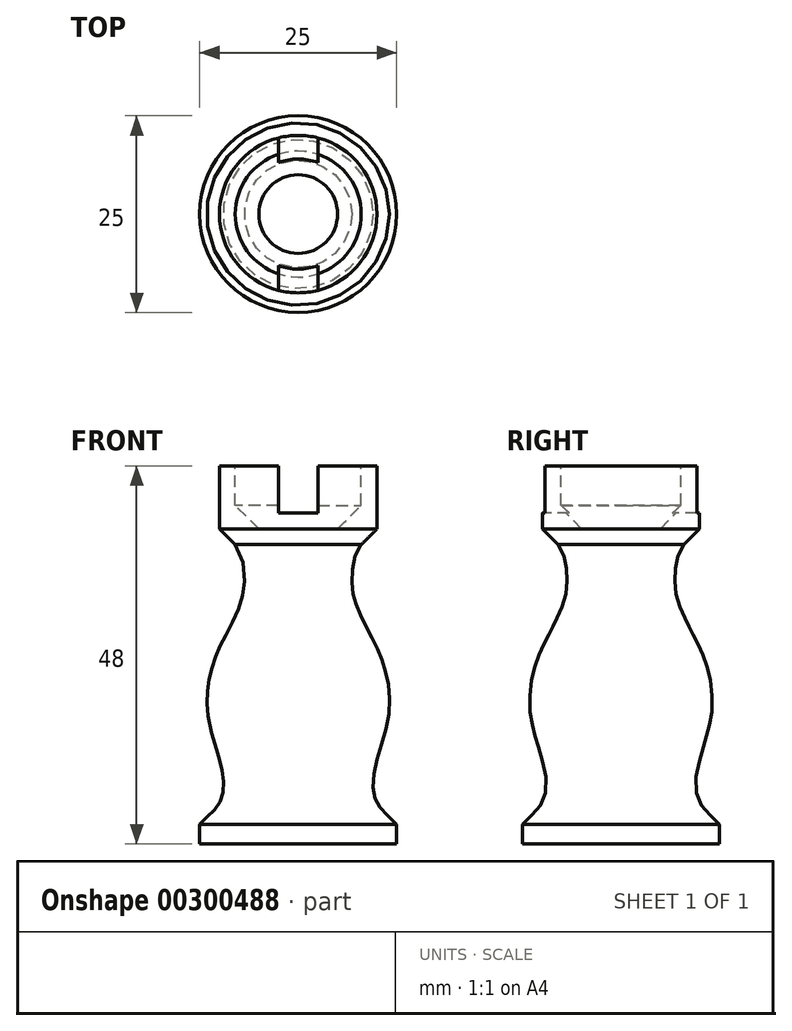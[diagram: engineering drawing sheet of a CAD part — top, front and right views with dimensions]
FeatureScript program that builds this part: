
annotation { "Feature Type Name" : "Feature", "Feature Type Description" : "" }
export const myFeature = defineFeature(function(context is Context, id is Id, definition is map)
    precondition{}
    {
        {
            var Q0;
            Q0=qCreatedBy(makeId("Front.planeOp"),FACE);
            var sketch = newSketch(context, id + "F0", { "sketchPlane" : qUnion([Q0])});
            skLineSegment(sketch, "E0.bottom", {"start": v(0, 0) * mm, "end": v(12.5, 0) * mm});
            skLineSegment(sketch, "E0.top", {"start": v(0, 48) * mm, "end": v(12.5, 48) * mm});
            skLineSegment(sketch, "E0.left", {"start": v(0, 0) * mm, "end": v(0, 48) * mm});
            skLineSegment(sketch, "E0.right", {"start": v(12.5, 0) * mm, "end": v(12.5, 48) * mm});
            skLineSegment(sketch, "E1.bottom", {"start": v(0, 48) * mm, "end": v(8, 48) * mm});
            skLineSegment(sketch, "E1.top", {"start": v(0, 40) * mm, "end": v(8, 40) * mm});
            skLineSegment(sketch, "E1.left", {"start": v(0, 48) * mm, "end": v(0, 40) * mm});
            skLineSegment(sketch, "E1.right", {"start": v(8, 48) * mm, "end": v(8, 40) * mm});
            skLineSegment(sketch, "E2", {"start": v(10, 48) * mm, "end": v(10, 38) * mm});
            skLineSegment(sketch, "E3", {"start": v(10, 38) * mm, "end": v(0, 38) * mm});
            skLineSegment(sketch, "E4", {"start": v(10, 40) * mm, "end": v(8, 38) * mm});
            skLineSegment(sketch, "E5", {"start": v(0, 2.5) * mm, "end": v(12.5, 2.5) * mm});
            skFitSpline(sketch, "E6", {"points": [v(8, 38) * mm, v(6.84, 33.3) * mm, v(7.56, 29.92) * mm, v(9.58, 25.78) * mm, v(11.1, 21.87) * mm, v(11.46, 16.18) * mm, v(9.68, 9.37) * mm, v(10, 5.2) * mm, v(12.5, 2.5) * mm], "startDerivative": vector(-23.17, -26.5) * mm, "endDerivative": vector(26.84, -29.85) * mm});
            skSolve(sketch);
        }
        {
            var Q0;
            {var subQ0=sQuery(id+"F0.wireOp",EDGE,"E1.top");Q0=makeQuery(id+"F0.imprint","IMPRINT",FACE,{"disambiguationData":[TD([[makeQuery(id+"F0.imprint","IMPRINT",EDGE,{"derivedFrom":subQ0}),-1.0]])]});}
            var Q1;
            {var subQ3=sQuery(id+"F0.wireOp",EDGE,"E5");Q1=makeQuery(id+"F0.imprint","IMPRINT",FACE,{"disambiguationData":[TD([[makeQuery(id+"F0.imprint","IMPRINT",EDGE,{"derivedFrom":subQ3}),1.0]])]});}
            var Q2;
            {var subQ0=sQuery(id+"F0.wireOp",EDGE,"E0.bottom");Q2=makeQuery(id+"F0.imprint","IMPRINT",FACE,{"disambiguationData":[TD([[makeQuery(id+"F0.imprint","IMPRINT",EDGE,{"derivedFrom":subQ0}),1.0]])]});}
            var Q3;
            Q3=sQuery(id+"F0.wireOp",EDGE,"E1.left");
            revolve(context, id + "F1", {"entities" : qUnion([Q0, Q1, Q2]), "axis" : qUnion([Q3]), "revolveType" : RevolveType.FULL});
        }
        {
            var Q0;
            Q0=makeQuery(id+"F1.opRevolve","SWEPT_FACE",FACE,{"disambiguationData":[OSD([sQuery(id+"F0.wireOp",EDGE,"E0.top")])]});
            var sketch = newSketch(context, id + "F2", { "sketchPlane" : qUnion([Q0])});
            skLineSegment(sketch, "E7.bottom", {"start": v(-2.5, 15) * mm, "end": v(2.5, 15) * mm});
            skLineSegment(sketch, "E7.top", {"start": v(-2.5, -15) * mm, "end": v(2.5, -15) * mm});
            skLineSegment(sketch, "E7.left", {"start": v(-2.5, 15) * mm, "end": v(-2.5, -15) * mm});
            skLineSegment(sketch, "E7.right", {"start": v(2.5, 15) * mm, "end": v(2.5, -15) * mm});
            skPoint(sketch, "E7.middle", {"position": v(0, 0) * mm});
            skSolve(sketch);
        }
        {
            var Q0;
            Q0 = qSketchRegion(id + "F2", true);
            extrude(context, id + "F3", {"entities" : qUnion([Q0]), "operationType" : NewBodyOperationType.REMOVE, "oppositeDirection" : true, "depth" : 6 * mm});
        }
        {
            var Q0;
            Q0=makeQuery(id+"F1.opRevolve","SWEPT_EDGE",EDGE,{"disambiguationData":[OSD([sQuery(id+"F0.wireOp",EDGE,"E1.top"),sQuery(id+"F0.wireOp",EDGE,"E1.right")])]});
            chamfer(context, id + "F4", {"entities" : qUnion([Q0]), "width" : 3 * mm, "tangentPropagation" : true});
        }
    });
